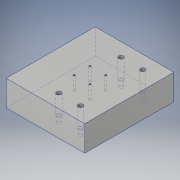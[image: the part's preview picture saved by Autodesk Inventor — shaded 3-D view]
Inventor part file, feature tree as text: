
AUTODESK INVENTOR PART (.ipt)
format: ipt  version: 2019.4 (Build 234330000, 330)  size: 125,440 bytes
history: native  units: in
note: dims shown in document units (in); Inventor stores cm internally (conversion verified against a paired STEP export)
features: sketch x3, hole x2, extrude x1
ambient origin geometry x8: Origin, YZ Plane, XZ Plane, XY Plane, X Axis, Y Axis, Z Axis, Center Point
bodies: Solid1 (feature_tree)
feature tree (6):
  extrude  "Extrusion1"  Depth=5.9055in
  hole  "Hole1"  [1 undecoded]
  hole  "Hole2"  [1 undecoded]
  sketch  "Sketch1"  dims[d0=6.6929in d1=5.9055in]
  sketch  "Sketch2"  dims[d2=1.92in d3=0.0in d4=0.5906in]
  sketch  "Sketch3"  dims[d5=0.5906in d6=0.7874in d8=1.1811in d9=0.7874in d11=1.1811in d14=0.1276in d15=0.315in d16=0.3701in d17=0.0787in d18=90.0deg d19=1.0in d20=0.8108in d21=1.012in d22=1.328in d23=0.7874in d25=4.67in d26=0.7874in d28=1.625in d31=0.266in d32=0.315in d33=0.34in d34=1.45in d35=90.0deg d36=1.0in d37=0.8108in]
note: 2 required parameter values undecoded (feature->parameter linkage not recoverable at this tier; creation-order binding heuristic only, values carry confidence <= 0.55)
